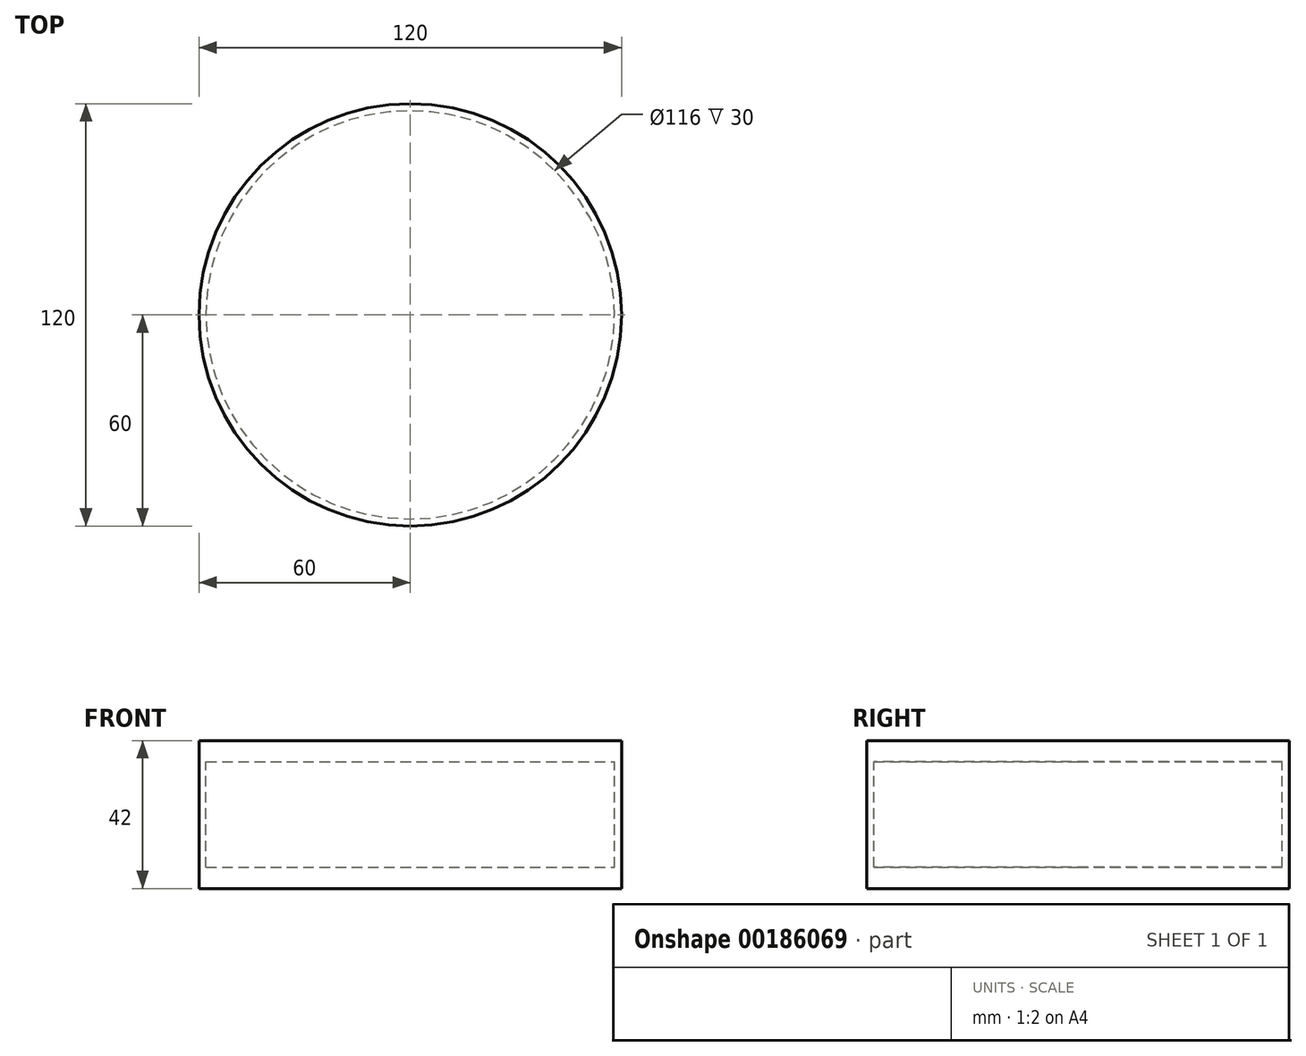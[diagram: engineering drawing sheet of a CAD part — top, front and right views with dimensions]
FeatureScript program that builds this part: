
annotation { "Feature Type Name" : "Feature", "Feature Type Description" : "" }
export const myFeature = defineFeature(function(context is Context, id is Id, definition is map)
    precondition{}
    {
        {
            var Q0;
            Q0=qCreatedBy(makeId("Top.planeOp"),FACE);
            var sketch = newSketch(context, id + "F0", { "sketchPlane" : qUnion([Q0])});
            skCircle(sketch, "E0", {"center": v(0, 0) * mm, "radius": 60 * mm});
            skSolve(sketch);
        }
        {
            var Q0;
            Q0 = qSketchRegion(id + "F0", true);
            extrude(context, id + "F1", {"entities" : qUnion([Q0]), "depth" : 6 * mm});
        }
        {
            var Q0;
            Q0=makeQuery(id+"F1.opExtrude","CAP_FACE",FACE,{"disambiguationData":[OSD([sQuery(id+"F0.wireOp",EDGE,"E0")])],"isStart":true});
            var sketch = newSketch(context, id + "F2", { "sketchPlane" : qUnion([Q0])});
            skCircle(sketch, "E1", {"center": v(0, 0) * mm, "radius": 60 * mm});
            skCircle(sketch, "E2", {"center": v(0, 0) * mm, "radius": 58 * mm});
            skSolve(sketch);
        }
        {
            var Q0;
            Q0=makeQuery(id+"F2.imprint","IMPRINT",FACE,{"disambiguationData":[TD([[makeQuery(id+"F2.imprint","IMPRINT",EDGE,{"derivedFrom":sQuery(id+"F2.wireOp",EDGE,"E1")}),-1.0]])]});
            extrude(context, id + "F3", {"entities" : qUnion([Q0]), "operationType" : NewBodyOperationType.ADD, "depth" : 30 * mm});
        }
        {
            var Q0;
            Q0=makeQuery(id+"F3.opExtrude","CAP_FACE",FACE,{"disambiguationData":[OSD([sQuery(id+"F2.wireOp",EDGE,"E1"),sQuery(id+"F2.wireOp",EDGE,"E2")])],"isStart":false});
            var sketch = newSketch(context, id + "F4", { "sketchPlane" : qUnion([Q0])});
            skCircle(sketch, "E3", {"center": v(0, 0) * mm, "radius": 60 * mm});
            skSolve(sketch);
        }
        {
            var Q0;
            Q0 = qSketchRegion(id + "F4", true);
            extrude(context, id + "F5", {"entities" : qUnion([Q0]), "operationType" : NewBodyOperationType.ADD, "depth" : 6 * mm});
        }
    });
